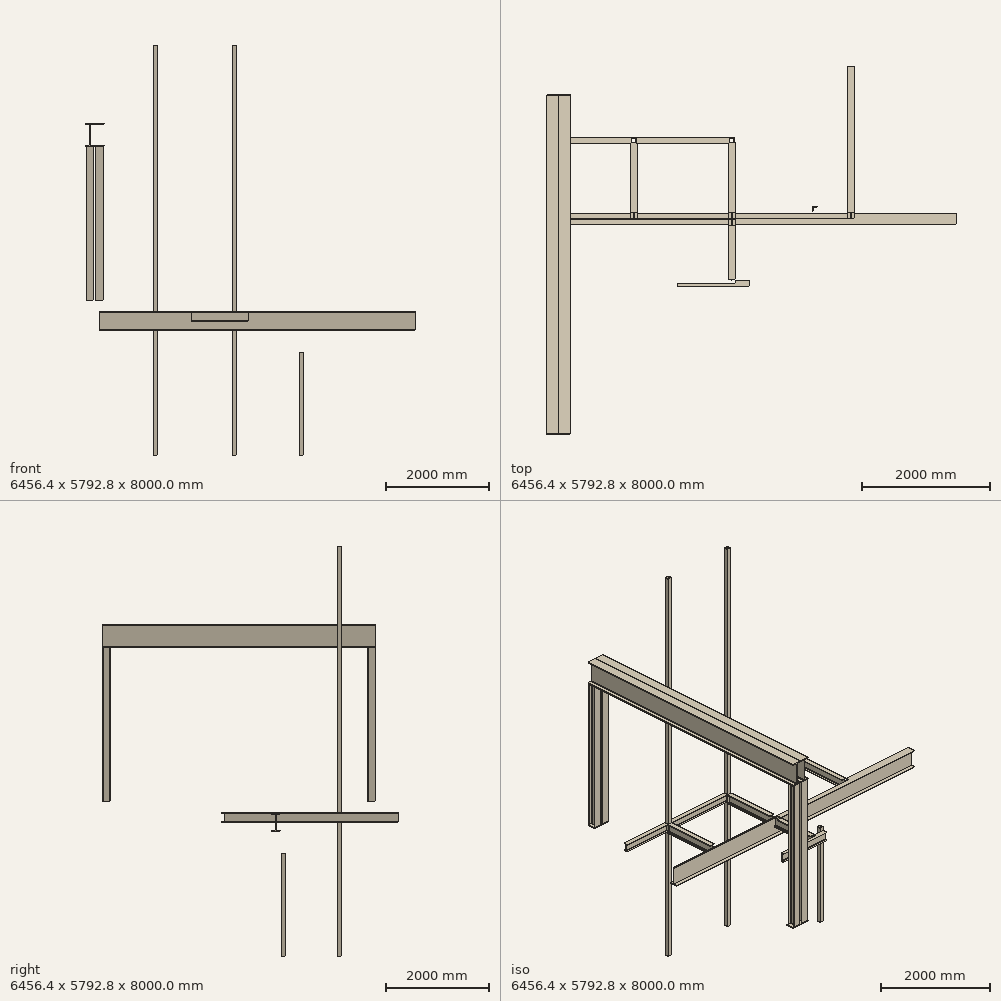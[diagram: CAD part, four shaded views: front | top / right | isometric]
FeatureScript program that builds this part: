
annotation { "Feature Type Name" : "Feature", "Feature Type Description" : "" }
export const myFeature = defineFeature(function(context is Context, id is Id, definition is map)
    precondition{}
    {
        {
            var Q0;
            Q0=qCreatedBy(makeId("Top.planeOp"),FACE);
            var sketch = newSketch(context, id + "F0", { "sketchPlane" : qUnion([Q0])});
            skLineSegment(sketch, "E0.bottom", {"start": v(-2000, 1060) * mm, "end": v(2000, 1060) * mm, "construction": true});
            skLineSegment(sketch, "E0.left", {"start": v(-2000, 1060) * mm, "end": v(-2000, -1240) * mm, "construction": true});
            skLineSegment(sketch, "E0.right", {"start": v(2000, 1060) * mm, "end": v(2000, -1240) * mm, "construction": true});
            skPoint(sketch, "E1", {"position": v(0, 0) * mm});
            skLineSegment(sketch, "E2", {"start": v(-1000, 1047.5) * mm, "end": v(-1000, -1240) * mm, "construction": true});
            skLineSegment(sketch, "E3", {"start": v(-2000, 0) * mm, "end": v(2990, 0) * mm, "construction": true});
            skLineSegment(sketch, "E4", {"start": v(-1000, 0) * mm, "end": v(-1715.91, -1240) * mm, "construction": true});
            skLineSegment(sketch, "E5", {"start": v(-1000, 0) * mm, "end": v(-2000, -577.35) * mm, "construction": true});
            skLineSegment(sketch, "E6", {"start": v(-1000, 0) * mm, "end": v(-2000, 0) * mm, "construction": true});
            skLineSegment(sketch, "E7.MirrorCS", {"start": v(-1000, 0) * mm, "end": v(-2000, 577.35) * mm, "construction": true});
            skLineSegment(sketch, "E8.MirrorCS", {"start": v(-1000, 0) * mm, "end": v(-1612, 1060) * mm, "construction": true});
            skLineSegment(sketch, "E9.bottom", {"start": v(-960, -40) * mm, "end": v(-1040, -40) * mm});
            skLineSegment(sketch, "E9.top", {"start": v(-960, 40) * mm, "end": v(-1040, 40) * mm});
            skLineSegment(sketch, "E9.left", {"start": v(-960, -40) * mm, "end": v(-960, 40) * mm});
            skLineSegment(sketch, "E9.right", {"start": v(-1040, -40) * mm, "end": v(-1040, 40) * mm});
            skPoint(sketch, "E9.middle", {"position": v(-1000, 0) * mm});
            skLineSegment(sketch, "E10.0", {"start": v(-968, 32) * mm, "end": v(-1032, 32) * mm});
            skLineSegment(sketch, "E11.0", {"start": v(-968, -32) * mm, "end": v(-1032, -32) * mm});
            skLineSegment(sketch, "E12.0", {"start": v(-1032, -32) * mm, "end": v(-1032, 32) * mm});
            skLineSegment(sketch, "E13.0", {"start": v(-968, -32) * mm, "end": v(-968, 32) * mm});
            skLineSegment(sketch, "E14.1.0.0", {"start": v(574, 32) * mm, "end": v(510, 32) * mm});
            skLineSegment(sketch, "E14.1.0.1", {"start": v(574, -32) * mm, "end": v(510, -32) * mm});
            skLineSegment(sketch, "E14.1.0.2", {"start": v(510, -32) * mm, "end": v(510, 32) * mm});
            skLineSegment(sketch, "E14.1.0.3", {"start": v(582, -40) * mm, "end": v(582, 40) * mm});
            skLineSegment(sketch, "E14.1.0.4", {"start": v(582, -40) * mm, "end": v(502, -40) * mm});
            skLineSegment(sketch, "E14.1.0.5", {"start": v(502, -40) * mm, "end": v(502, 40) * mm});
            skLineSegment(sketch, "E14.1.0.6", {"start": v(582, 40) * mm, "end": v(502, 40) * mm});
            skLineSegment(sketch, "E14.1.0.7", {"start": v(574, -32) * mm, "end": v(574, 32) * mm});
            skPoint(sketch, "E14.1.0.8", {"position": v(542, 0) * mm});
            skLineSegment(sketch, "E15.0", {"start": v(2080, 1060) * mm, "end": v(2080, -1240) * mm, "construction": true});
            skLineSegment(sketch, "E16.0", {"start": v(542, 1060) * mm, "end": v(542, -1240) * mm, "construction": true});
            skLineSegment(sketch, "E17.0", {"start": v(-2000, -1240) * mm, "end": v(2000, -1240) * mm, "construction": true});
            skPoint(sketch, "E18", {"position": v(1855, -1090) * mm});
            skLineSegment(sketch, "E19.bottom", {"start": v(1895, -1130) * mm, "end": v(1815, -1130) * mm});
            skLineSegment(sketch, "E19.top", {"start": v(1895, -1050) * mm, "end": v(1815, -1050) * mm});
            skLineSegment(sketch, "E19.left", {"start": v(1895, -1130) * mm, "end": v(1895, -1050) * mm});
            skLineSegment(sketch, "E19.right", {"start": v(1815, -1130) * mm, "end": v(1815, -1050) * mm});
            skLineSegment(sketch, "E20.0", {"start": v(1887, -1058) * mm, "end": v(1823, -1058) * mm});
            skLineSegment(sketch, "E21.0", {"start": v(1887, -1122) * mm, "end": v(1823, -1122) * mm});
            skLineSegment(sketch, "E22.0", {"start": v(1823, -1122) * mm, "end": v(1823, -1058) * mm});
            skLineSegment(sketch, "E23.0", {"start": v(1887, -1122) * mm, "end": v(1887, -1058) * mm});
            skLineSegment(sketch, "E24.0", {"start": v(-2000, -2260) * mm, "end": v(2000, -2260) * mm, "construction": true});
            skSolve(sketch);
        }
        {
            var Q0;
            Q0=makeQuery(id+"F0.imprint","IMPRINT",FACE,{"disambiguationData":[TD([[makeQuery(id+"F0.imprint","IMPRINT",EDGE,{"derivedFrom":sQuery(id+"F0.wireOp",EDGE,"E9.bottom")}),-1.0]])]});
            var Q1;
            Q1=makeQuery(id+"F0.imprint","IMPRINT",FACE,{"disambiguationData":[TD([[makeQuery(id+"F0.imprint","IMPRINT",EDGE,{"derivedFrom":sQuery(id+"F0.wireOp",EDGE,"E14.1.0.0")}),-1.0]])]});
            extrude(context, id + "F1", {"entities" : qUnion([Q0, Q1]), "depth" : 8000 * mm, "offsetDistance" : 25 * mm});
        }
        {
            var Q0;
            Q0=makeQuery(id+"F0.imprint","IMPRINT",FACE,{"disambiguationData":[TD([[makeQuery(id+"F0.imprint","IMPRINT",EDGE,{"derivedFrom":sQuery(id+"F0.wireOp",EDGE,"E19.bottom")}),-1.0]])]});
            extrude(context, id + "F2", {"entities" : qUnion([Q0]), "depth" : 2000 * mm, "offsetDistance" : 25 * mm});
        }
        {
            var Q0;
            Q0=qCreatedBy(makeId("Top.planeOp"),FACE);
            cPlane(context, id + "F3", {"entities" : qUnion([Q0]), "cplaneType" : CPlaneType.OFFSET, "offset" : 3000 * mm, "width" : 150 * mm, "height" : 150 * mm});
        }
        {
            var Q0;
            Q0=qCreatedBy(id+"F3.planeOp",FACE);
            var sketch = newSketch(context, id + "F4", { "sketchPlane" : qUnion([Q0])});
            skLineSegment(sketch, "E25.bottom", {"start": v(-2000, 1060) * mm, "end": v(2000, 1060) * mm, "construction": true});
            skLineSegment(sketch, "E25.left", {"start": v(-2000, 1060) * mm, "end": v(-2000, -1240) * mm, "construction": true});
            skLineSegment(sketch, "E25.right", {"start": v(2000, 1060) * mm, "end": v(2000, -1240) * mm, "construction": true});
            skPoint(sketch, "E26", {"position": v(0, 0) * mm});
            skLineSegment(sketch, "E27", {"start": v(-1000, 1047.5) * mm, "end": v(-1000, -1240) * mm, "construction": true});
            skLineSegment(sketch, "E28", {"start": v(-2000, 0) * mm, "end": v(2990, 0) * mm, "construction": true});
            skLineSegment(sketch, "E29", {"start": v(-1000, 0) * mm, "end": v(-1715.91, -1240) * mm, "construction": true});
            skLineSegment(sketch, "E30", {"start": v(-1000, 0) * mm, "end": v(-2000, -577.35) * mm, "construction": true});
            skLineSegment(sketch, "E31", {"start": v(-1000, 0) * mm, "end": v(-2000, 0) * mm, "construction": true});
            skLineSegment(sketch, "E32.MirrorCS", {"start": v(-1000, 0) * mm, "end": v(-2000, 577.35) * mm, "construction": true});
            skLineSegment(sketch, "E33.MirrorCS", {"start": v(-1000, 0) * mm, "end": v(-1612, 1060) * mm, "construction": true});
            skLineSegment(sketch, "E34.0", {"start": v(2080, 1060) * mm, "end": v(2080, -1240) * mm, "construction": true});
            skLineSegment(sketch, "E35.0", {"start": v(542, 1060) * mm, "end": v(542, -1240) * mm, "construction": true});
            skLineSegment(sketch, "E36.0", {"start": v(-2000, -1240) * mm, "end": v(2000, -1240) * mm, "construction": true});
            skPoint(sketch, "E37", {"position": v(1855, -1090) * mm});
            skLineSegment(sketch, "E38.0", {"start": v(-2000, -2260) * mm, "end": v(2000, -2260) * mm, "construction": true});
            skLineSegment(sketch, "E39", {"start": v(-1761.65, 631) * mm, "end": v(-4300.92, 631) * mm, "construction": true});
            skLineSegment(sketch, "E40.0", {"start": v(-1761.65, -4544) * mm, "end": v(-4300.92, -4544) * mm, "construction": true});
            skLineSegment(sketch, "E41.0", {"start": v(-2047, 1047.5) * mm, "end": v(-2047, -4544) * mm, "construction": true});
            skSolve(sketch);
        }
        {
            var Q0;
            Q0=qCreatedBy(id+"F3.planeOp",FACE);
            cPlane(context, id + "F5", {"entities" : qUnion([Q0]), "cplaneType" : CPlaneType.OFFSET, "offset" : 2000 * mm, "width" : 150 * mm, "height" : 150 * mm});
        }
        {
            var Q0;
            Q0=qCreatedBy(id+"F5.planeOp",FACE);
            cPlane(context, id + "F6", {"entities" : qUnion([Q0]), "cplaneType" : CPlaneType.OFFSET, "offset" : 2000 * mm, "width" : 150 * mm, "height" : 150 * mm});
        }
        {
            var Q0;
            Q0=qCreatedBy(id+"F6.planeOp",FACE);
            cPlane(context, id + "F7", {"entities" : qUnion([Q0]), "cplaneType" : CPlaneType.OFFSET, "offset" : 2000 * mm, "width" : 150 * mm, "height" : 150 * mm});
        }
        {
            var Q0;
            Q0=qCreatedBy(makeId("Right.planeOp"),FACE);
            cPlane(context, id + "F8", {"entities" : qUnion([Q0]), "cplaneType" : CPlaneType.OFFSET, "offset" : 2080 * mm, "width" : 150 * mm, "height" : 150 * mm});
        }
        {
            var Q0;
            Q0=qCreatedBy(id+"F8.planeOp",FACE);
            var sketch = newSketch(context, id + "F9", { "sketchPlane" : qUnion([Q0])});
            skLineSegment(sketch, "E42", {"start": v(-1325.55, 2800) * mm, "end": v(-1154.45, 2800) * mm});
            skLineSegment(sketch, "E43", {"start": v(-1154.45, 2800) * mm, "end": v(-1154.45, 2790.3) * mm});
            skLineSegment(sketch, "E44", {"start": v(-1154.45, 2790.3) * mm, "end": v(-1236.5, 2790.3) * mm});
            skLineSegment(sketch, "E45", {"start": v(-1236.5, 2790.3) * mm, "end": v(-1236.5, 2458.3) * mm});
            skLineSegment(sketch, "E46", {"start": v(-1236.5, 2458.3) * mm, "end": v(-1154.45, 2458.3) * mm});
            skLineSegment(sketch, "E47", {"start": v(-1154.45, 2458.3) * mm, "end": v(-1154.45, 2448.6) * mm});
            skLineSegment(sketch, "E48", {"start": v(-1154.45, 2448.6) * mm, "end": v(-1325.55, 2448.6) * mm});
            skLineSegment(sketch, "E49", {"start": v(-1325.55, 2448.6) * mm, "end": v(-1325.55, 2458.3) * mm});
            skLineSegment(sketch, "E50", {"start": v(-1325.55, 2458.3) * mm, "end": v(-1243.5, 2458.3) * mm});
            skLineSegment(sketch, "E51", {"start": v(-1243.5, 2458.3) * mm, "end": v(-1243.5, 2790.3) * mm});
            skLineSegment(sketch, "E52", {"start": v(-1243.5, 2790.3) * mm, "end": v(-1325.55, 2790.3) * mm});
            skLineSegment(sketch, "E53", {"start": v(-1325.55, 2790.3) * mm, "end": v(-1325.55, 2800) * mm});
            skLineSegment(sketch, "E54", {"start": v(-1232.41, 2800) * mm, "end": v(1088.94, 2800) * mm, "construction": true});
            skLineSegment(sketch, "E55", {"start": v(-1240, 2281.76) * mm, "end": v(-1240, 1619.13) * mm, "construction": true});
            skPoint(sketch, "E56", {"position": v(-1240, 2800) * mm});
            skSolve(sketch);
        }
        {
            var Q0;
            Q0 = qSketchRegion(id + "F9", true);
            extrude(context, id + "F10", {"entities" : qUnion([Q0]), "depth" : 2000 * mm, "offsetDistance" : 25 * mm, "hasSecondDirection" : true, "secondDirectionOppositeDirection" : true, "secondDirectionDepth" : 4180 * mm});
        }
        {
            var Q0;
            Q0=qCreatedBy(makeId("Front.planeOp"),FACE);
            cPlane(context, id + "F11", {"entities" : qUnion([Q0]), "cplaneType" : CPlaneType.OFFSET, "offset" : 1060 * mm, "oppositeDirection" : true, "width" : 150 * mm, "height" : 150 * mm});
        }
        {
            var Q0;
            Q0=qCreatedBy(id+"F11.planeOp",FACE);
            var sketch = newSketch(context, id + "F12", { "sketchPlane" : qUnion([Q0])});
            skLineSegment(sketch, "E57", {"start": v(2470.92, 2800) * mm, "end": v(2369.72, 2800) * mm});
            skLineSegment(sketch, "E58", {"start": v(2369.72, 2800) * mm, "end": v(2369.72, 2792.1) * mm});
            skLineSegment(sketch, "E59", {"start": v(2369.72, 2792.1) * mm, "end": v(2410.32, 2792.1) * mm});
            skLineSegment(sketch, "E60", {"start": v(2417.92, 2784.5) * mm, "end": v(2417.92, 2637.7) * mm});
            skLineSegment(sketch, "E61", {"start": v(2410.32, 2630.1) * mm, "end": v(2369.72, 2630.1) * mm});
            skLineSegment(sketch, "E62", {"start": v(2369.72, 2630.1) * mm, "end": v(2369.72, 2622.2) * mm});
            skLineSegment(sketch, "E63", {"start": v(2369.72, 2622.2) * mm, "end": v(2470.92, 2622.2) * mm});
            skLineSegment(sketch, "E64", {"start": v(2470.92, 2622.2) * mm, "end": v(2470.92, 2630.1) * mm});
            skLineSegment(sketch, "E65", {"start": v(2470.92, 2630.1) * mm, "end": v(2430.32, 2630.1) * mm});
            skLineSegment(sketch, "E66", {"start": v(2422.72, 2637.7) * mm, "end": v(2422.72, 2784.5) * mm});
            skLineSegment(sketch, "E67", {"start": v(2430.32, 2792.1) * mm, "end": v(2470.92, 2792.1) * mm});
            skLineSegment(sketch, "E68", {"start": v(2470.92, 2792.1) * mm, "end": v(2470.92, 2800) * mm});
            skPoint(sketch, "E69.visualSharp", {"position": v(2417.92, 2792.1) * mm});
            skArc(sketch, "E69.filletArc", {"start": v(2417.92, 2784.5) * mm, "mid": v(2415.7, 2789.87) * mm, "end": v(2410.32, 2792.1) * mm});
            skPoint(sketch, "E70.visualSharp", {"position": v(2417.92, 2630.1) * mm});
            skArc(sketch, "E70.filletArc", {"start": v(2410.32, 2630.1) * mm, "mid": v(2415.7, 2632.33) * mm, "end": v(2417.92, 2637.7) * mm});
            skPoint(sketch, "E71.visualSharp", {"position": v(2422.72, 2630.1) * mm});
            skArc(sketch, "E71.filletArc", {"start": v(2422.72, 2637.7) * mm, "mid": v(2424.95, 2632.33) * mm, "end": v(2430.32, 2630.1) * mm});
            skPoint(sketch, "E72.visualSharp", {"position": v(2422.72, 2792.1) * mm});
            skArc(sketch, "E72.filletArc", {"start": v(2430.32, 2792.1) * mm, "mid": v(2424.95, 2789.87) * mm, "end": v(2422.72, 2784.5) * mm});
            skPoint(sketch, "E73", {"position": v(2420.32, 2800) * mm});
            skLineSegment(sketch, "E74", {"start": v(2233.76, 2866.96) * mm, "end": v(2553.41, 2866.96) * mm, "construction": true});
            skSolve(sketch);
        }
        {
            var Q0;
            Q0 = qSketchRegion(id + "F12", true);
            extrude(context, id + "F13", {"entities" : qUnion([Q0]), "depth" : (2300 - 13) * mm, "offsetDistance" : 25 * mm, "hasSecondDirection" : true, "secondDirectionOppositeDirection" : true, "secondDirectionDepth" : 100 * mm});
        }
        {
            var Q0;
            Q0=makeQuery(id+"F13.opExtrude","SWEPT_FACE",FACE,{"disambiguationData":[OSD([sQuery(id+"F12.wireOp",EDGE,"E68")])]});
            var sketch = newSketch(context, id + "F14", { "sketchPlane" : qUnion([Q0])});
            skLineSegment(sketch, "E75", {"start": v(-1227, 2780.3) * mm, "end": v(-1154.45, 2780.3) * mm});
            skLineSegment(sketch, "E76", {"start": v(-1144.45, 2790.3) * mm, "end": v(-1144.45, 2800) * mm});
            skLineSegment(sketch, "E77", {"start": v(-1144.45, 2800) * mm, "end": v(-1227, 2800) * mm});
            skLineSegment(sketch, "E78", {"start": v(-1227, 2800) * mm, "end": v(-1227, 2780.3) * mm});
            skPoint(sketch, "E79.visualSharp", {"position": v(-1144.45, 2780.3) * mm});
            skArc(sketch, "E79.filletArc", {"start": v(-1154.45, 2780.3) * mm, "mid": v(-1147.38, 2783.23) * mm, "end": v(-1144.45, 2790.3) * mm});
            skSolve(sketch);
        }
        {
            var Q0;
            Q0 = qSketchRegion(id + "F14", true);
            extrude(context, id + "F15", {"entities" : qUnion([Q0]), "operationType" : NewBodyOperationType.REMOVE, "endBound" : BoundingType.THROUGH_ALL, "oppositeDirection" : true, "depth" : 25 * mm, "offsetDistance" : 25 * mm});
        }
        {
            var Q0;
            Q0=makeQuery(id+"F1.opExtrude","SWEPT_FACE",FACE,{"disambiguationData":[OSD([sQuery(id+"F0.wireOp",EDGE,"E14.1.0.4")])]});
            var sketch = newSketch(context, id + "F16", { "sketchPlane" : qUnion([Q0])});
            skLineSegment(sketch, "E80", {"start": v(592.6, 2800) * mm, "end": v(491.4, 2800) * mm});
            skLineSegment(sketch, "E81", {"start": v(491.4, 2800) * mm, "end": v(491.4, 2792.1) * mm});
            skLineSegment(sketch, "E82", {"start": v(538.4, 2784.5) * mm, "end": v(538.4, 2637.7) * mm});
            skLineSegment(sketch, "E83", {"start": v(530.8, 2630.1) * mm, "end": v(491.4, 2630.1) * mm});
            skLineSegment(sketch, "E84", {"start": v(491.4, 2630.1) * mm, "end": v(491.4, 2622.2) * mm});
            skLineSegment(sketch, "E85", {"start": v(491.4, 2622.2) * mm, "end": v(592.6, 2622.2) * mm});
            skLineSegment(sketch, "E86", {"start": v(592.6, 2622.2) * mm, "end": v(592.6, 2630.1) * mm});
            skLineSegment(sketch, "E87", {"start": v(592.6, 2630.1) * mm, "end": v(553.2, 2630.1) * mm});
            skPoint(sketch, "E88.visualSharp", {"position": v(538.4, 2630.1) * mm});
            skArc(sketch, "E88.filletArc", {"start": v(530.8, 2630.1) * mm, "mid": v(536.17, 2632.33) * mm, "end": v(538.4, 2637.7) * mm});
            skPoint(sketch, "E89.visualSharp", {"position": v(544.4, 1630.1) * mm});
            skArc(sketch, "E89.filletArc", {"start": v(545.6, 2637.7) * mm, "mid": v(547.83, 2632.33) * mm, "end": v(553.2, 2630.1) * mm});
            skPoint(sketch, "E90", {"position": v(542, 2800) * mm});
            skLineSegment(sketch, "E91", {"start": v(502, 2800) * mm, "end": v(582, 2800) * mm, "construction": true});
            skLineSegment(sketch, "E92", {"start": v(542, 1826.12) * mm, "end": v(542, 2800) * mm, "construction": true});
            skLineSegment(sketch, "E93", {"start": v(592.6, 2792.1) * mm, "end": v(592.6, 2800) * mm});
            skLineSegment(sketch, "E94", {"start": v(545.6, 2637.7) * mm, "end": v(545.6, 2784.5) * mm});
            skArc(sketch, "E95.filletArc", {"start": v(538.4, 2784.5) * mm, "mid": v(536.17, 2789.87) * mm, "end": v(530.8, 2792.1) * mm});
            skLineSegment(sketch, "E96", {"start": v(491.4, 2792.1) * mm, "end": v(530.8, 2792.1) * mm});
            skLineSegment(sketch, "E97", {"start": v(592.6, 2792.1) * mm, "end": v(553.2, 2792.1) * mm});
            skPoint(sketch, "E98.visualSharp", {"position": v(545.6, 2792.1) * mm});
            skArc(sketch, "E98.filletArc", {"start": v(553.2, 2792.1) * mm, "mid": v(547.83, 2789.87) * mm, "end": v(545.6, 2784.5) * mm});
            skSolve(sketch);
        }
        {
            var Q0;
            Q0 = qSketchRegion(id + "F16", true);
            extrude(context, id + "F17", {"entities" : qUnion([Q0]), "depth" : 1187 * mm, "offsetDistance" : 25 * mm});
        }
        {
            var Q0;
            Q0=makeQuery(id+"F17.opExtrude","SWEPT_FACE",FACE,{"disambiguationData":[OSD([sQuery(id+"F16.wireOp",EDGE,"E93")])]});
            var sketch = newSketch(context, id + "F18", { "sketchPlane" : qUnion([Q0])});
            skLineSegment(sketch, "E99.bottom", {"start": v(-1227, 2800) * mm, "end": v(-1144.45, 2800) * mm});
            skLineSegment(sketch, "E99.top", {"start": v(-1227, 2780.3) * mm, "end": v(-1154.45, 2780.3) * mm});
            skLineSegment(sketch, "E99.left", {"start": v(-1227, 2800) * mm, "end": v(-1227, 2780.3) * mm});
            skLineSegment(sketch, "E99.right", {"start": v(-1144.45, 2800) * mm, "end": v(-1144.45, 2790.3) * mm});
            skPoint(sketch, "E100.visualSharp", {"position": v(-1144.45, 2780.3) * mm});
            skArc(sketch, "E100.filletArc", {"start": v(-1154.45, 2780.3) * mm, "mid": v(-1147.38, 2783.23) * mm, "end": v(-1144.45, 2790.3) * mm});
            skSolve(sketch);
        }
        {
            var Q0;
            Q0 = qSketchRegion(id + "F18", true);
            extrude(context, id + "F19", {"entities" : qUnion([Q0]), "operationType" : NewBodyOperationType.REMOVE, "endBound" : BoundingType.THROUGH_ALL, "oppositeDirection" : true, "depth" : 25 * mm, "offsetDistance" : 25 * mm});
        }
        {
            var Q0;
            Q0=makeQuery(id+"F17.opExtrude","SWEPT_BODY",BODY,{"disambiguationData":[OSD([sQuery(id+"F16.wireOp",EDGE,"E80"),sQuery(id+"F16.wireOp",EDGE,"E81"),sQuery(id+"F16.wireOp",EDGE,"E82"),sQuery(id+"F16.wireOp",EDGE,"E83"),sQuery(id+"F16.wireOp",EDGE,"E84"),sQuery(id+"F16.wireOp",EDGE,"E85"),sQuery(id+"F16.wireOp",EDGE,"E86"),sQuery(id+"F16.wireOp",EDGE,"E87"),sQuery(id+"F16.wireOp",EDGE,"E88.filletArc"),sQuery(id+"F16.wireOp",EDGE,"E89.filletArc"),sQuery(id+"F16.wireOp",EDGE,"E93"),sQuery(id+"F16.wireOp",EDGE,"E94"),sQuery(id+"F16.wireOp",EDGE,"E95.filletArc"),sQuery(id+"F16.wireOp",EDGE,"E96"),sQuery(id+"F16.wireOp",EDGE,"E97"),sQuery(id+"F16.wireOp",EDGE,"E98.filletArc")])]});
            transform(context, id + "F20", {"entities" : qUnion([Q0]), "transformType" : TransformType.TRANSLATION_3D, "dx" : -1542 * mm, "dy" : 0 * mm, "dz" : 0 * mm, "makeCopy" : true});
        }
        {
            var Q0;
            Q0=makeQuery(id+"F1.opExtrude","SWEPT_FACE",FACE,{"disambiguationData":[OSD([sQuery(id+"F0.wireOp",EDGE,"E9.left")])]});
            var sketch = newSketch(context, id + "F21", { "sketchPlane" : qUnion([Q0])});
            skLineSegment(sketch, "E101", {"start": v(-44.35, 2800) * mm, "end": v(44.35, 2800) * mm});
            skLineSegment(sketch, "E102", {"start": v(44.35, 2800) * mm, "end": v(44.35, 2792.3) * mm});
            skLineSegment(sketch, "E103", {"start": v(44.35, 2792.3) * mm, "end": v(9.85, 2792.3) * mm});
            skLineSegment(sketch, "E104", {"start": v(2.25, 2784.7) * mm, "end": v(2.25, 2662.9) * mm});
            skLineSegment(sketch, "E105", {"start": v(9.85, 2655.3) * mm, "end": v(44.35, 2655.3) * mm});
            skLineSegment(sketch, "E106", {"start": v(44.35, 2655.3) * mm, "end": v(44.35, 2647.6) * mm});
            skLineSegment(sketch, "E107", {"start": v(44.35, 2647.6) * mm, "end": v(-44.35, 2647.6) * mm});
            skLineSegment(sketch, "E108", {"start": v(-44.35, 2647.6) * mm, "end": v(-44.35, 2655.3) * mm});
            skLineSegment(sketch, "E109", {"start": v(-44.35, 2655.3) * mm, "end": v(-9.85, 2655.3) * mm});
            skLineSegment(sketch, "E110", {"start": v(-2.25, 2662.9) * mm, "end": v(-2.25, 2784.7) * mm});
            skLineSegment(sketch, "E111", {"start": v(-9.85, 2792.3) * mm, "end": v(-44.35, 2792.3) * mm});
            skLineSegment(sketch, "E112", {"start": v(-44.35, 2792.3) * mm, "end": v(-44.35, 2800) * mm});
            skPoint(sketch, "E113.visualSharp", {"position": v(2.25, 2792.3) * mm});
            skArc(sketch, "E113.filletArc", {"start": v(9.85, 2792.3) * mm, "mid": v(4.48, 2790.07) * mm, "end": v(2.25, 2784.7) * mm});
            skPoint(sketch, "E114.visualSharp", {"position": v(2.25, 2655.3) * mm});
            skArc(sketch, "E114.filletArc", {"start": v(2.25, 2662.9) * mm, "mid": v(4.48, 2657.53) * mm, "end": v(9.85, 2655.3) * mm});
            skPoint(sketch, "E115.visualSharp", {"position": v(-2.25, 2655.3) * mm});
            skArc(sketch, "E115.filletArc", {"start": v(-9.85, 2655.3) * mm, "mid": v(-4.48, 2657.53) * mm, "end": v(-2.25, 2662.9) * mm});
            skPoint(sketch, "E116.visualSharp", {"position": v(-2.25, 2792.3) * mm});
            skArc(sketch, "E116.filletArc", {"start": v(-2.25, 2784.7) * mm, "mid": v(-4.48, 2790.07) * mm, "end": v(-9.85, 2792.3) * mm});
            skLineSegment(sketch, "E117", {"start": v(-40, 2800) * mm, "end": v(40, 2800) * mm, "construction": true});
            skLineSegment(sketch, "E118", {"start": v(40, 2800) * mm, "end": v(0, 2800) * mm, "construction": true});
            skLineSegment(sketch, "E119", {"start": v(0, 1853.74) * mm, "end": v(0, 2800) * mm, "construction": true});
            skPoint(sketch, "E120", {"position": v(0, 2800) * mm});
            skSolve(sketch);
        }
        {
            var Q0;
            Q0 = qSketchRegion(id + "F21", true);
            extrude(context, id + "F22", {"entities" : qUnion([Q0]), "depth" : 1462 * mm, "offsetDistance" : 25 * mm});
        }
        {
            var Q0;
            Q0=makeQuery(id+"F1.opExtrude","SWEPT_FACE",FACE,{"disambiguationData":[OSD([sQuery(id+"F0.wireOp",EDGE,"E9.right")])]});
            var sketch = newSketch(context, id + "F23", { "sketchPlane" : qUnion([Q0])});
            skLineSegment(sketch, "E121", {"start": v(-44.35, 2800) * mm, "end": v(44.35, 2800) * mm});
            skLineSegment(sketch, "E122", {"start": v(44.35, 2800) * mm, "end": v(44.35, 2792.3) * mm});
            skLineSegment(sketch, "E123", {"start": v(44.35, 2792.3) * mm, "end": v(9.85, 2792.3) * mm});
            skLineSegment(sketch, "E124", {"start": v(2.25, 2784.7) * mm, "end": v(2.25, 2662.9) * mm});
            skLineSegment(sketch, "E125", {"start": v(9.85, 2655.3) * mm, "end": v(44.35, 2655.3) * mm});
            skLineSegment(sketch, "E126", {"start": v(44.35, 2655.3) * mm, "end": v(44.35, 2647.6) * mm});
            skLineSegment(sketch, "E127", {"start": v(44.35, 2647.6) * mm, "end": v(-44.35, 2647.6) * mm});
            skLineSegment(sketch, "E128", {"start": v(-44.35, 2647.6) * mm, "end": v(-44.35, 2655.3) * mm});
            skLineSegment(sketch, "E129", {"start": v(-44.35, 2655.3) * mm, "end": v(-9.85, 2655.3) * mm});
            skLineSegment(sketch, "E130", {"start": v(-2.25, 2662.9) * mm, "end": v(-2.25, 2784.7) * mm});
            skLineSegment(sketch, "E131", {"start": v(-9.85, 2792.3) * mm, "end": v(-44.35, 2792.3) * mm});
            skLineSegment(sketch, "E132", {"start": v(-44.35, 2792.3) * mm, "end": v(-44.35, 2800) * mm});
            skPoint(sketch, "E133.visualSharp", {"position": v(2.25, 2792.3) * mm});
            skArc(sketch, "E133.filletArc", {"start": v(9.85, 2792.3) * mm, "mid": v(4.48, 2790.07) * mm, "end": v(2.25, 2784.7) * mm});
            skPoint(sketch, "E134.visualSharp", {"position": v(2.25, 2655.3) * mm});
            skArc(sketch, "E134.filletArc", {"start": v(2.25, 2662.9) * mm, "mid": v(4.48, 2657.53) * mm, "end": v(9.85, 2655.3) * mm});
            skPoint(sketch, "E135.visualSharp", {"position": v(-2.25, 2655.3) * mm});
            skArc(sketch, "E135.filletArc", {"start": v(-9.85, 2655.3) * mm, "mid": v(-4.48, 2657.53) * mm, "end": v(-2.25, 2662.9) * mm});
            skPoint(sketch, "E136.visualSharp", {"position": v(-2.25, 2792.3) * mm});
            skArc(sketch, "E136.filletArc", {"start": v(-2.25, 2784.7) * mm, "mid": v(-4.48, 2790.07) * mm, "end": v(-9.85, 2792.3) * mm});
            skLineSegment(sketch, "E137", {"start": v(-40, 2800) * mm, "end": v(40, 2800) * mm, "construction": true});
            skLineSegment(sketch, "E138", {"start": v(40, 2800) * mm, "end": v(0, 2800) * mm, "construction": true});
            skLineSegment(sketch, "E139", {"start": v(0, 2008.32) * mm, "end": v(0, 2800) * mm, "construction": true});
            skPoint(sketch, "E140", {"position": v(0, 2800) * mm});
            skLineSegment(sketch, "E141", {"start": v(-40, 2800) * mm, "end": v(40, 2800) * mm});
            skLineSegment(sketch, "E142", {"start": v(40, 2800) * mm, "end": v(0, 2800) * mm});
            skLineSegment(sketch, "E143", {"start": v(0, 1859.93) * mm, "end": v(0, 2800) * mm});
            skSolve(sketch);
        }
        {
            var Q0;
            Q0 = qSketchRegion(id + "F23", true);
            extrude(context, id + "F24", {"entities" : qUnion([Q0]), "depth" : 1060 * mm, "offsetDistance" : 25 * mm});
        }
        {
            var Q0;
            Q0=qCreatedBy(makeId("Right.planeOp"),FACE);
            cPlane(context, id + "F25", {"entities" : qUnion([Q0]), "cplaneType" : CPlaneType.OFFSET, "offset" : 817 * mm, "width" : 150 * mm, "height" : 150 * mm});
        }
        {
            var Q0;
            Q0=qCreatedBy(id+"F25.planeOp",FACE);
            var sketch = newSketch(context, id + "F26", { "sketchPlane" : qUnion([Q0])});
            skLineSegment(sketch, "E144", {"start": v(-2209.4, 2800) * mm, "end": v(-2310.6, 2800) * mm});
            skLineSegment(sketch, "E145", {"start": v(-2310.6, 2800) * mm, "end": v(-2310.6, 2792.1) * mm});
            skLineSegment(sketch, "E146", {"start": v(-2264.8, 2784.89) * mm, "end": v(-2264.8, 2637.7) * mm});
            skLineSegment(sketch, "E147", {"start": v(-2272.4, 2630.1) * mm, "end": v(-2310.6, 2630.1) * mm});
            skLineSegment(sketch, "E148", {"start": v(-2310.6, 2630.1) * mm, "end": v(-2310.6, 2622.2) * mm});
            skLineSegment(sketch, "E149", {"start": v(-2310.6, 2622.2) * mm, "end": v(-2209.4, 2622.2) * mm});
            skLineSegment(sketch, "E150", {"start": v(-2209.4, 2622.2) * mm, "end": v(-2209.4, 2630.1) * mm});
            skLineSegment(sketch, "E151", {"start": v(-2209.4, 2630.1) * mm, "end": v(-2250, 2630.1) * mm});
            skPoint(sketch, "E152.visualSharp", {"position": v(-2264.8, 2630.1) * mm});
            skArc(sketch, "E152.filletArc", {"start": v(-2272.4, 2630.1) * mm, "mid": v(-2267.03, 2632.33) * mm, "end": v(-2264.8, 2637.7) * mm});
            skPoint(sketch, "E153.visualSharp", {"position": v(-2257.6, 2630.1) * mm});
            skArc(sketch, "E153.filletArc", {"start": v(-2257.6, 2637.7) * mm, "mid": v(-2255.37, 2632.33) * mm, "end": v(-2250, 2630.1) * mm});
            skPoint(sketch, "E154", {"position": v(-2260, 2800) * mm});
            skLineSegment(sketch, "E155", {"start": v(-2300, 2800) * mm, "end": v(-2220, 2800) * mm, "construction": true});
            skLineSegment(sketch, "E156", {"start": v(-2260, 2800) * mm, "end": v(-2260, 2826.12) * mm, "construction": true});
            skLineSegment(sketch, "E157", {"start": v(-2209.4, 2792.1) * mm, "end": v(-2209.4, 2800) * mm});
            skLineSegment(sketch, "E158", {"start": v(-2257.6, 2637.7) * mm, "end": v(-2257.6, 2784.5) * mm});
            skArc(sketch, "E159.filletArc", {"start": v(-2264.8, 2784.89) * mm, "mid": v(-2266.24, 2789.33) * mm, "end": v(-2270, 2792.1) * mm});
            skLineSegment(sketch, "E160", {"start": v(-2310.6, 2792.1) * mm, "end": v(-2270, 2792.1) * mm});
            skLineSegment(sketch, "E161", {"start": v(-2209.4, 2792.1) * mm, "end": v(-2250, 2792.1) * mm});
            skPoint(sketch, "E162.visualSharp", {"position": v(-2257.6, 2792.1) * mm});
            skArc(sketch, "E162.filletArc", {"start": v(-2250, 2792.1) * mm, "mid": v(-2255.37, 2789.87) * mm, "end": v(-2257.6, 2784.5) * mm});
            skLineSegment(sketch, "E163", {"start": v(-1240, 2800) * mm, "end": v(-2250, 2800) * mm, "construction": true});
            skLineSegment(sketch, "E164", {"start": v(-2260, 2017.11) * mm, "end": v(-2260, 1627.77) * mm, "construction": true});
            skSolve(sketch);
        }
        {
            var Q0;
            Q0 = qSketchRegion(id + "F26", true);
            extrude(context, id + "F27", {"entities" : qUnion([Q0]), "oppositeDirection" : true, "depth" : 1126 * mm, "offsetDistance" : 25 * mm});
        }
        {
            var Q0;
            Q0=qCreatedBy(id+"F3.planeOp",FACE);
            cPlane(context, id + "F28", {"entities" : qUnion([Q0]), "cplaneType" : CPlaneType.OFFSET, "offset" : 25 * mm, "width" : 150 * mm, "height" : 150 * mm});
        }
        {
            var Q0;
            Q0=qCreatedBy(id+"F28.planeOp",FACE);
            var sketch = newSketch(context, id + "F29", { "sketchPlane" : qUnion([Q0])});
            skLineSegment(sketch, "E165.0", {"start": v(-2090, 1047.5) * mm, "end": v(-2090, -4867.74) * mm});
            skLineSegment(sketch, "E166.0", {"start": v(-2280, 1047.5) * mm, "end": v(-2280, -4867.74) * mm});
            skLineSegment(sketch, "E167", {"start": v(-4261.2, -4544) * mm, "end": v(-1078.23, -4544) * mm});
            skLineSegment(sketch, "E168", {"start": v(-4579.67, 631) * mm, "end": v(-359.07, 631) * mm});
            skLineSegment(sketch, "E169", {"start": v(-2356.45, 709.8) * mm, "end": v(-2203.55, 709.8) * mm});
            skLineSegment(sketch, "E170", {"start": v(-2203.55, 709.8) * mm, "end": v(-2203.55, 703) * mm});
            skLineSegment(sketch, "E171", {"start": v(-2203.55, 703) * mm, "end": v(-2269.5, 703) * mm});
            skLineSegment(sketch, "E172", {"start": v(-2277.1, 695.4) * mm, "end": v(-2277.1, 566.6) * mm});
            skLineSegment(sketch, "E173", {"start": v(-2269.5, 559) * mm, "end": v(-2203.55, 559) * mm});
            skLineSegment(sketch, "E174", {"start": v(-2203.55, 559) * mm, "end": v(-2203.55, 552.2) * mm});
            skLineSegment(sketch, "E175", {"start": v(-2203.55, 552.2) * mm, "end": v(-2356.45, 552.2) * mm});
            skLineSegment(sketch, "E176", {"start": v(-2356.45, 552.2) * mm, "end": v(-2356.45, 559) * mm});
            skLineSegment(sketch, "E177", {"start": v(-2356.45, 559) * mm, "end": v(-2290.5, 559) * mm});
            skLineSegment(sketch, "E178", {"start": v(-2282.9, 566.6) * mm, "end": v(-2282.9, 695.4) * mm});
            skLineSegment(sketch, "E179", {"start": v(-2290.5, 703) * mm, "end": v(-2356.45, 703) * mm});
            skLineSegment(sketch, "E180", {"start": v(-2356.45, 703) * mm, "end": v(-2356.45, 709.8) * mm});
            skPoint(sketch, "E181", {"position": v(-2280, 709.8) * mm});
            skPoint(sketch, "E182.visualSharp", {"position": v(-2277.1, 703) * mm});
            skArc(sketch, "E182.filletArc", {"start": v(-2269.5, 703) * mm, "mid": v(-2274.87, 700.77) * mm, "end": v(-2277.1, 695.4) * mm});
            skPoint(sketch, "E183.visualSharp", {"position": v(-2282.9, 703) * mm});
            skArc(sketch, "E183.filletArc", {"start": v(-2282.9, 695.4) * mm, "mid": v(-2285.13, 700.77) * mm, "end": v(-2290.5, 703) * mm});
            skPoint(sketch, "E184.visualSharp", {"position": v(-2282.9, 559) * mm});
            skArc(sketch, "E184.filletArc", {"start": v(-2290.5, 559) * mm, "mid": v(-2285.13, 561.23) * mm, "end": v(-2282.9, 566.6) * mm});
            skPoint(sketch, "E185.visualSharp", {"position": v(-2277.1, 559) * mm});
            skArc(sketch, "E185.filletArc", {"start": v(-2277.1, 566.6) * mm, "mid": v(-2274.87, 561.23) * mm, "end": v(-2269.5, 559) * mm});
            skPoint(sketch, "E186", {"position": v(-2280, 631) * mm});
            skPoint(sketch, "E187", {"position": v(-2090, 631) * mm});
            skLineSegment(sketch, "E188", {"start": v(-2356.45, 552.2) * mm, "end": v(-2203.55, 709.8) * mm, "construction": true});
            skLineSegment(sketch, "E189.direction1", {"start": v(-2356.45, 552.2) * mm, "end": v(-2166.45, 552.2) * mm, "construction": true});
            skLineSegment(sketch, "E190", {"start": v(-3293.75, 631) * mm, "end": v(-3293.75, -4544) * mm});
            skLineSegment(sketch, "E191", {"start": v(-3293.75, -1956.5) * mm, "end": v(-4944.68, -1956.5) * mm});
            skSolve(sketch);
        }
        {
            var Q0;
            {var subQ0=sQuery(id+"F29.wireOp",EDGE,"E170");Q0=makeQuery(id+"F29.imprint","IMPRINT",FACE,{"disambiguationData":[TD([[makeQuery(id+"F29.imprint","IMPRINT",EDGE,{"derivedFrom":subQ0}),-1.0]])]});}
            var Q1;
            Q1=makeQuery(id+"F29.imprint","IMPRINT",FACE,{"disambiguationData":[TD([[makeQuery(id+"F29.imprint","IMPRINT",EDGE,{"derivedFrom":sQuery(id+"F29.wireOp",EDGE,"E179")}),-1.0]])]});
            var Q2;
            {var subQ0=sQuery(id+"F29.wireOp",EDGE,"E176");Q2=makeQuery(id+"F29.imprint","IMPRINT",FACE,{"disambiguationData":[TD([[makeQuery(id+"F29.imprint","IMPRINT",EDGE,{"derivedFrom":subQ0}),-1.0]])]});}
            var Q3;
            Q3=makeQuery(id+"F29.imprint","IMPRINT",FACE,{"disambiguationData":[TD([[makeQuery(id+"F29.imprint","IMPRINT",EDGE,{"derivedFrom":sQuery(id+"F29.wireOp",EDGE,"E173")}),-1.0]])]});
            extrude(context, id + "F30", {"entities" : qUnion([Q0, Q1, Q2, Q3]), "depth" : 3000 * mm, "offsetDistance" : 25 * mm});
        }
        {
            var Q0;
            Q0=makeQuery(id+"F30.opExtrude","SWEPT_BODY",BODY,{"disambiguationData":[OSD([sQuery(id+"F29.wireOp",EDGE,"E169"),sQuery(id+"F29.wireOp",EDGE,"E170"),sQuery(id+"F29.wireOp",EDGE,"E171"),sQuery(id+"F29.wireOp",EDGE,"E172"),sQuery(id+"F29.wireOp",EDGE,"E173"),sQuery(id+"F29.wireOp",EDGE,"E174"),sQuery(id+"F29.wireOp",EDGE,"E175"),sQuery(id+"F29.wireOp",EDGE,"E176"),sQuery(id+"F29.wireOp",EDGE,"E177"),sQuery(id+"F29.wireOp",EDGE,"E178"),sQuery(id+"F29.wireOp",EDGE,"E179"),sQuery(id+"F29.wireOp",EDGE,"E180"),sQuery(id+"F29.wireOp",EDGE,"E182.filletArc"),sQuery(id+"F29.wireOp",EDGE,"E183.filletArc"),sQuery(id+"F29.wireOp",EDGE,"E184.filletArc"),sQuery(id+"F29.wireOp",EDGE,"E185.filletArc")])]});
            transform(context, id + "F31", {"entities" : qUnion([Q0]), "transformType" : TransformType.TRANSLATION_3D, "dx" : 190 * mm, "dy" : 0 * mm, "dz" : 0 * mm, "makeCopy" : true});
        }
        {
            var Q0;
            Q0=makeQuery(id+"F30.opExtrude","SWEPT_BODY",BODY,{"disambiguationData":[OSD([sQuery(id+"F29.wireOp",EDGE,"E169"),sQuery(id+"F29.wireOp",EDGE,"E170"),sQuery(id+"F29.wireOp",EDGE,"E171"),sQuery(id+"F29.wireOp",EDGE,"E172"),sQuery(id+"F29.wireOp",EDGE,"E173"),sQuery(id+"F29.wireOp",EDGE,"E174"),sQuery(id+"F29.wireOp",EDGE,"E175"),sQuery(id+"F29.wireOp",EDGE,"E176"),sQuery(id+"F29.wireOp",EDGE,"E177"),sQuery(id+"F29.wireOp",EDGE,"E178"),sQuery(id+"F29.wireOp",EDGE,"E179"),sQuery(id+"F29.wireOp",EDGE,"E180"),sQuery(id+"F29.wireOp",EDGE,"E182.filletArc"),sQuery(id+"F29.wireOp",EDGE,"E183.filletArc"),sQuery(id+"F29.wireOp",EDGE,"E184.filletArc"),sQuery(id+"F29.wireOp",EDGE,"E185.filletArc")])]});
            var Q1;
            Q1=makeQuery(id+"F31.opPattern","COPY",BODY,{"derivedFrom":makeQuery(id+"F30.opExtrude","SWEPT_BODY",BODY,{"disambiguationData":[OSD([sQuery(id+"F29.wireOp",EDGE,"E169"),sQuery(id+"F29.wireOp",EDGE,"E170"),sQuery(id+"F29.wireOp",EDGE,"E171"),sQuery(id+"F29.wireOp",EDGE,"E172"),sQuery(id+"F29.wireOp",EDGE,"E173"),sQuery(id+"F29.wireOp",EDGE,"E174"),sQuery(id+"F29.wireOp",EDGE,"E175"),sQuery(id+"F29.wireOp",EDGE,"E176"),sQuery(id+"F29.wireOp",EDGE,"E177"),sQuery(id+"F29.wireOp",EDGE,"E178"),sQuery(id+"F29.wireOp",EDGE,"E179"),sQuery(id+"F29.wireOp",EDGE,"E180"),sQuery(id+"F29.wireOp",EDGE,"E182.filletArc"),sQuery(id+"F29.wireOp",EDGE,"E183.filletArc"),sQuery(id+"F29.wireOp",EDGE,"E184.filletArc"),sQuery(id+"F29.wireOp",EDGE,"E185.filletArc")])]}),"instanceName":"1"});
            var Q2;
            Q2=sQuery(id+"F4.wireOp",EDGE,"E41.0");
            transform(context, id + "F32", {"entities" : qUnion([Q0, Q1]), "transformType" : TransformType.TRANSLATION_3D, "dx" : 0 * mm, "dy" : -5175 * mm, "dz" : 0 * mm, "makeCopy" : true});
        }
        {
            var Q0;
            Q0=makeQuery(id+"F32.opPattern","COPY",FACE,{"derivedFrom":makeQuery(id+"F30.opExtrude","SWEPT_FACE",FACE,{"disambiguationData":[OSD([sQuery(id+"F29.wireOp",EDGE,"E175")])]}),"instanceName":"1"});
            var sketch = newSketch(context, id + "F33", { "sketchPlane" : qUnion([Q0])});
            skLineSegment(sketch, "E192", {"start": v(-2185.83, 6482) * mm, "end": v(-1995.83, 6482) * mm});
            skLineSegment(sketch, "E193", {"start": v(-1995.83, 6482) * mm, "end": v(-1995.83, 6467.5) * mm});
            skLineSegment(sketch, "E194", {"start": v(-1995.83, 6467.5) * mm, "end": v(-2076.13, 6467.5) * mm});
            skLineSegment(sketch, "E195", {"start": v(-2086.33, 6457.3) * mm, "end": v(-2086.33, 6049.7) * mm});
            skLineSegment(sketch, "E196", {"start": v(-2076.13, 6039.5) * mm, "end": v(-1995.83, 6039.5) * mm});
            skLineSegment(sketch, "E197", {"start": v(-1995.83, 6039.5) * mm, "end": v(-1995.83, 6025) * mm});
            skLineSegment(sketch, "E198", {"start": v(-1995.83, 6025) * mm, "end": v(-2185.83, 6025) * mm});
            skLineSegment(sketch, "E199", {"start": v(-2185.83, 6025) * mm, "end": v(-2185.83, 6039.5) * mm});
            skLineSegment(sketch, "E200", {"start": v(-2185.83, 6039.5) * mm, "end": v(-2105.53, 6039.5) * mm});
            skLineSegment(sketch, "E201", {"start": v(-2095.33, 6049.7) * mm, "end": v(-2095.33, 6457.3) * mm});
            skLineSegment(sketch, "E202", {"start": v(-2105.53, 6467.5) * mm, "end": v(-2185.83, 6467.5) * mm});
            skLineSegment(sketch, "E203", {"start": v(-2185.83, 6467.5) * mm, "end": v(-2185.83, 6482) * mm});
            skPoint(sketch, "E204.visualSharp", {"position": v(-2086.33, 6467.5) * mm});
            skArc(sketch, "E204.filletArc", {"start": v(-2076.13, 6467.5) * mm, "mid": v(-2083.34, 6464.51) * mm, "end": v(-2086.33, 6457.3) * mm});
            skPoint(sketch, "E205.visualSharp", {"position": v(-2095.33, 6467.5) * mm});
            skArc(sketch, "E205.filletArc", {"start": v(-2095.33, 6457.3) * mm, "mid": v(-2098.32, 6464.51) * mm, "end": v(-2105.53, 6467.5) * mm});
            skPoint(sketch, "E206.visualSharp", {"position": v(-2095.33, 6039.5) * mm});
            skArc(sketch, "E206.filletArc", {"start": v(-2105.53, 6039.5) * mm, "mid": v(-2098.32, 6042.49) * mm, "end": v(-2095.33, 6049.7) * mm});
            skPoint(sketch, "E207.visualSharp", {"position": v(-2086.33, 6039.5) * mm});
            skArc(sketch, "E207.filletArc", {"start": v(-2086.33, 6049.7) * mm, "mid": v(-2083.34, 6042.49) * mm, "end": v(-2076.13, 6039.5) * mm});
            skPoint(sketch, "E208", {"position": v(-2108.55, 5035) * mm});
            skSolve(sketch);
        }
        {
            var Q0;
            Q0 = qSketchRegion(id + "F33", true);
            extrude(context, id + "F34", {"entities" : qUnion([Q0]), "oppositeDirection" : true, "depth" : 5332.6 * mm, "offsetDistance" : 25 * mm});
        }
        {
            var Q0;
            Q0=makeQuery(id+"F32.opPattern","COPY",FACE,{"derivedFrom":makeQuery(id+"F30.opExtrude","CAP_FACE",FACE,{"disambiguationData":[OSD([sQuery(id+"F29.wireOp",EDGE,"E169"),sQuery(id+"F29.wireOp",EDGE,"E170"),sQuery(id+"F29.wireOp",EDGE,"E171"),sQuery(id+"F29.wireOp",EDGE,"E172"),sQuery(id+"F29.wireOp",EDGE,"E173"),sQuery(id+"F29.wireOp",EDGE,"E174"),sQuery(id+"F29.wireOp",EDGE,"E175"),sQuery(id+"F29.wireOp",EDGE,"E176"),sQuery(id+"F29.wireOp",EDGE,"E177"),sQuery(id+"F29.wireOp",EDGE,"E178"),sQuery(id+"F29.wireOp",EDGE,"E179"),sQuery(id+"F29.wireOp",EDGE,"E180"),sQuery(id+"F29.wireOp",EDGE,"E182.filletArc"),sQuery(id+"F29.wireOp",EDGE,"E183.filletArc"),sQuery(id+"F29.wireOp",EDGE,"E184.filletArc"),sQuery(id+"F29.wireOp",EDGE,"E185.filletArc")])],"isStart":false}),"instanceName":"1"});
            var sketch = newSketch(context, id + "F35", { "sketchPlane" : qUnion([Q0])});
            skLineSegment(sketch, "E209.bottom", {"start": v(-2376.45, -4455.2) * mm, "end": v(-1993.55, -4455.2) * mm});
            skLineSegment(sketch, "E209.top", {"start": v(-2376.45, -4632.8) * mm, "end": v(-1993.55, -4632.8) * mm});
            skLineSegment(sketch, "E209.left", {"start": v(-2376.45, -4455.2) * mm, "end": v(-2376.45, -4632.8) * mm});
            skLineSegment(sketch, "E209.right", {"start": v(-1993.55, -4455.2) * mm, "end": v(-1993.55, -4632.8) * mm});
            skLineSegment(sketch, "E210.bottom", {"start": v(-2366.45, 719.8) * mm, "end": v(-2003.55, 719.8) * mm});
            skLineSegment(sketch, "E210.top", {"start": v(-2366.45, 542.2) * mm, "end": v(-2003.55, 542.2) * mm});
            skLineSegment(sketch, "E210.left", {"start": v(-2366.45, 719.8) * mm, "end": v(-2366.45, 542.2) * mm});
            skLineSegment(sketch, "E210.right", {"start": v(-2003.55, 719.8) * mm, "end": v(-2003.55, 542.2) * mm});
            skSolve(sketch);
        }
        {
            var Q0;
            Q0 = qSketchRegion(id + "F35", true);
            extrude(context, id + "F36", {"entities" : qUnion([Q0]), "depth" : 10 * mm, "offsetDistance" : 25 * mm});
        }
        {
            var Q0;
            Q0=makeQuery(id+"F34.opExtrude","SWEPT_BODY",BODY,{"disambiguationData":[OSD([sQuery(id+"F33.wireOp",EDGE,"E192"),sQuery(id+"F33.wireOp",EDGE,"E193"),sQuery(id+"F33.wireOp",EDGE,"E194"),sQuery(id+"F33.wireOp",EDGE,"E195"),sQuery(id+"F33.wireOp",EDGE,"E196"),sQuery(id+"F33.wireOp",EDGE,"E197"),sQuery(id+"F33.wireOp",EDGE,"E198"),sQuery(id+"F33.wireOp",EDGE,"E199"),sQuery(id+"F33.wireOp",EDGE,"E200"),sQuery(id+"F33.wireOp",EDGE,"E201"),sQuery(id+"F33.wireOp",EDGE,"E202"),sQuery(id+"F33.wireOp",EDGE,"E203"),sQuery(id+"F33.wireOp",EDGE,"E204.filletArc"),sQuery(id+"F33.wireOp",EDGE,"E205.filletArc"),sQuery(id+"F33.wireOp",EDGE,"E206.filletArc"),sQuery(id+"F33.wireOp",EDGE,"E207.filletArc")])]});
            transform(context, id + "F37", {"entities" : qUnion([Q0]), "transformType" : TransformType.TRANSLATION_3D, "dx" : -190 * mm, "dy" : 0 * mm, "dz" : 0 * mm, "makeCopy" : true});
        }
        {
            var Q0;
            Q0=makeQuery(id+"F36.opExtrude","SWEPT_BODY",BODY,{"disambiguationData":[OSD([sQuery(id+"F35.wireOp",EDGE,"E209.bottom"),sQuery(id+"F35.wireOp",EDGE,"E209.top"),sQuery(id+"F35.wireOp",EDGE,"E209.left"),sQuery(id+"F35.wireOp",EDGE,"E209.right")])]});
            var Q1;
            Q1=makeQuery(id+"F36.opExtrude","SWEPT_BODY",BODY,{"disambiguationData":[OSD([sQuery(id+"F35.wireOp",EDGE,"E210.bottom"),sQuery(id+"F35.wireOp",EDGE,"E210.top"),sQuery(id+"F35.wireOp",EDGE,"E210.left"),sQuery(id+"F35.wireOp",EDGE,"E210.right")])]});
            transform(context, id + "F38", {"entities" : qUnion([Q0, Q1]), "transformType" : TransformType.TRANSLATION_3D, "dx" : 0 * mm, "dy" : 0 * mm, "dz" : -3010 * mm, "makeCopy" : true});
        }
        {
            var Q0;
            Q0=makeQuery(id+"F10.opExtrude","SWEPT_FACE",FACE,{"disambiguationData":[OSD([sQuery(id+"F9.wireOp",EDGE,"E51")])]});
            cPlane(context, id + "F39", {"entities" : qUnion([Q0]), "cplaneType" : CPlaneType.OFFSET, "offset" : 10 * mm, "width" : 150 * mm, "height" : 150 * mm});
        }
        {
            var Q0;
            Q0=qCreatedBy(id+"F39.planeOp",FACE);
            var sketch = newSketch(context, id + "F40", { "sketchPlane" : qUnion([Q0])});
            skLineSegment(sketch, "E211", {"start": v(592.6, 2800) * mm, "end": v(491.4, 2800) * mm});
            skLineSegment(sketch, "E212", {"start": v(491.4, 2800) * mm, "end": v(491.4, 2792.1) * mm});
            skLineSegment(sketch, "E213", {"start": v(491.4, 2792.1) * mm, "end": v(532, 2792.1) * mm});
            skLineSegment(sketch, "E214", {"start": v(539.6, 2784.5) * mm, "end": v(539.6, 2637.7) * mm});
            skLineSegment(sketch, "E215", {"start": v(532, 2630.1) * mm, "end": v(491.4, 2630.1) * mm});
            skLineSegment(sketch, "E216", {"start": v(491.4, 2630.1) * mm, "end": v(491.4, 2622.2) * mm});
            skLineSegment(sketch, "E217", {"start": v(491.4, 2622.2) * mm, "end": v(592.6, 2622.2) * mm});
            skLineSegment(sketch, "E218", {"start": v(592.6, 2622.2) * mm, "end": v(592.6, 2630.1) * mm});
            skLineSegment(sketch, "E219", {"start": v(592.6, 2630.1) * mm, "end": v(552, 2630.1) * mm});
            skLineSegment(sketch, "E220", {"start": v(544.4, 2637.7) * mm, "end": v(544.4, 2784.5) * mm});
            skLineSegment(sketch, "E221", {"start": v(552, 2792.1) * mm, "end": v(592.6, 2792.1) * mm});
            skLineSegment(sketch, "E222", {"start": v(592.6, 2792.1) * mm, "end": v(592.6, 2800) * mm});
            skPoint(sketch, "E223.visualSharp", {"position": v(539.6, 2792.1) * mm});
            skArc(sketch, "E223.filletArc", {"start": v(539.6, 2784.5) * mm, "mid": v(537.37, 2789.87) * mm, "end": v(532, 2792.1) * mm});
            skPoint(sketch, "E224.visualSharp", {"position": v(539.6, 2630.1) * mm});
            skArc(sketch, "E224.filletArc", {"start": v(532, 2630.1) * mm, "mid": v(537.37, 2632.33) * mm, "end": v(539.6, 2637.7) * mm});
            skPoint(sketch, "E225.visualSharp", {"position": v(544.4, 2630.1) * mm});
            skArc(sketch, "E225.filletArc", {"start": v(544.4, 2637.7) * mm, "mid": v(546.63, 2632.33) * mm, "end": v(552, 2630.1) * mm});
            skPoint(sketch, "E226.visualSharp", {"position": v(544.4, 2792.1) * mm});
            skArc(sketch, "E226.filletArc", {"start": v(552, 2792.1) * mm, "mid": v(546.63, 2789.87) * mm, "end": v(544.4, 2784.5) * mm});
            skPoint(sketch, "E227", {"position": v(542, 2800) * mm});
            skLineSegment(sketch, "E228", {"start": v(634.26, 2052.6) * mm, "end": v(953.9, 2052.6) * mm, "construction": true});
            skSolve(sketch);
        }
        {
            var Q0;
            Q0 = qSketchRegion(id + "F40", true);
            extrude(context, id + "F41", {"entities" : qUnion([Q0]), "depth" : 995.9 * mm, "offsetDistance" : 25 * mm});
        }
        {
            var Q0;
            Q0=makeQuery(id+"F41.opExtrude","SWEPT_FACE",FACE,{"disambiguationData":[OSD([sQuery(id+"F40.wireOp",EDGE,"E222")])]});
            var sketch = newSketch(context, id + "F42", { "sketchPlane" : qUnion([Q0])});
            skLineSegment(sketch, "E229.bottom", {"start": v(-2249.4, 2800) * mm, "end": v(-2199.4, 2800) * mm});
            skLineSegment(sketch, "E229.top", {"start": v(-2249.4, 2782.1) * mm, "end": v(-2209.4, 2782.1) * mm});
            skLineSegment(sketch, "E229.left", {"start": v(-2249.4, 2800) * mm, "end": v(-2249.4, 2782.1) * mm});
            skLineSegment(sketch, "E229.right", {"start": v(-2199.4, 2800) * mm, "end": v(-2199.4, 2792.1) * mm});
            skPoint(sketch, "E230.visualSharp", {"position": v(-2199.4, 2782.1) * mm});
            skArc(sketch, "E230.filletArc", {"start": v(-2209.4, 2782.1) * mm, "mid": v(-2202.33, 2785.03) * mm, "end": v(-2199.4, 2792.1) * mm});
            skLineSegment(sketch, "E231.bottom", {"start": v(-2249.4, 2640.1) * mm, "end": v(-2209.4, 2640.1) * mm});
            skLineSegment(sketch, "E231.top", {"start": v(-2249.4, 1621.63) * mm, "end": v(-2199.4, 1621.63) * mm});
            skLineSegment(sketch, "E231.left", {"start": v(-2249.4, 2640.1) * mm, "end": v(-2249.4, 1621.63) * mm});
            skLineSegment(sketch, "E231.right", {"start": v(-2199.4, 2630.1) * mm, "end": v(-2199.4, 1621.63) * mm});
            skPoint(sketch, "E232.visualSharp", {"position": v(-2199.4, 2640.1) * mm});
            skArc(sketch, "E232.filletArc", {"start": v(-2199.4, 2630.1) * mm, "mid": v(-2202.33, 2637.17) * mm, "end": v(-2209.4, 2640.1) * mm});
            skLineSegment(sketch, "E233.bottom", {"start": v(-1335.55, 2800) * mm, "end": v(-1252.17, 2800) * mm});
            skLineSegment(sketch, "E233.top", {"start": v(-1325.55, 2780.3) * mm, "end": v(-1252.17, 2780.3) * mm});
            skLineSegment(sketch, "E233.left", {"start": v(-1335.55, 2800) * mm, "end": v(-1335.55, 2790.3) * mm});
            skLineSegment(sketch, "E233.right", {"start": v(-1252.17, 2800) * mm, "end": v(-1252.17, 2780.3) * mm});
            skPoint(sketch, "E234.visualSharp", {"position": v(-1335.55, 2780.3) * mm});
            skArc(sketch, "E234.filletArc", {"start": v(-1335.55, 2790.3) * mm, "mid": v(-1332.62, 2783.23) * mm, "end": v(-1325.55, 2780.3) * mm});
            skSolve(sketch);
        }
        {
            var Q0;
            Q0 = qSketchRegion(id + "F42", true);
            extrude(context, id + "F43", {"entities" : qUnion([Q0]), "operationType" : NewBodyOperationType.REMOVE, "endBound" : BoundingType.THROUGH_ALL, "oppositeDirection" : true, "depth" : 25 * mm, "offsetDistance" : 25 * mm});
        }
    });
